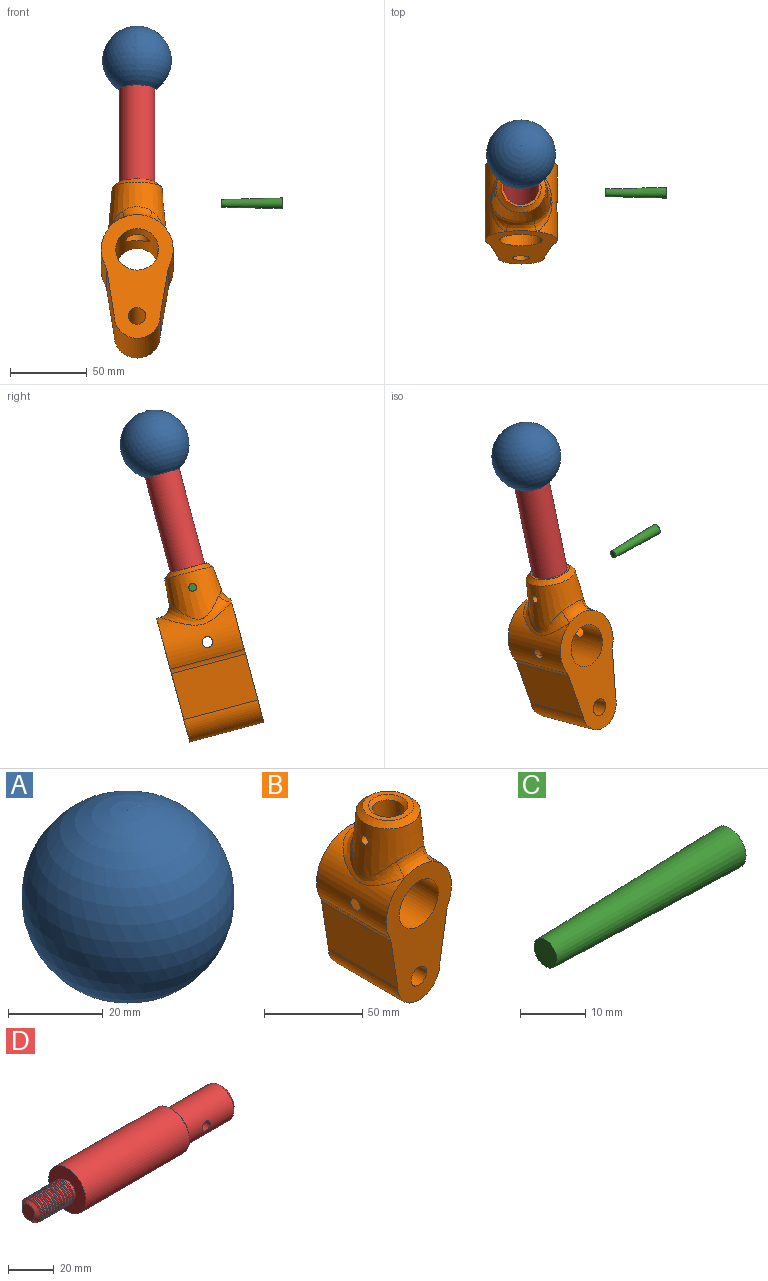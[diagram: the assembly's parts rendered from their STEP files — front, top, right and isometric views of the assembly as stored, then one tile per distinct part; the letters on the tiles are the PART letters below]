
ASSEMBLY  parts=4 mates=3
PART A: 8 faces, bbox 45.4x45.4x43.2 mm
  f0: sphere r=22.5mm, area 5937.6mm2, adj f1
  f1: plane 22.87x22.87mm, normal (0,0,-1), area 304.4mm2, adj f0,f3,f5,f6
  f2: cone r=0mm half-angle=59deg, axis (0,0,-1), area 97.2mm2, adj f3,f4
  f3: cylinder r=5.15mm len=34mm, axis (0,0,-1), area 433.4mm2, adj f1,f2,f5,f6,f7
  f4: cylinder r=5.15mm len=4.09mm, axis (0,0,1), area 0.6mm2, adj f2,f5,f7
  f5: bspline ~35.2x13.86mm, area 672mm2, adj f1,f3,f4,f6,f7
  f6: bspline ~34.62x13.86mm, area 657.8mm2, adj f1,f3,f5,f7
  f7: plane 0.98x0.68mm, normal (0.79,-0.61,0), area 0.4mm2, adj f3,f4,f5,f6
PART B: 21 faces, bbox 47x50x110 mm
  f0: cone r=16mm half-angle=5deg, axis (0,0,-1), area 2465.3mm2, adj f13,f14,f15,f19,f20
  f1: cylinder r=8mm len=36.51mm, axis (0,0,1), area 1715mm2, adj f2,f16,f19,f20
  f2: cylinder r=14mm len=50mm, axis (0,-1,0), area 4080.2mm2, adj f1,f8,f9,f17,f18
  f3: cylinder r=23.5mm len=50mm, axis (0,-1,0), area 2892.7mm2, adj f8,f9,f10,f11,f13,f17,f18
  f4: plane 50x31.11mm, normal (-0.99,0,-0.15), area 1574.5mm2, adj f5,f8,f9,f10
  f5: cylinder r=15mm len=50mm, axis (0,-1,0), area 2356.2mm2, adj f4,f6,f8,f9
  f6: plane 50x32.09mm, normal (0.99,0,-0.16), area 1626.1mm2, adj f5,f8,f9,f11
  f7: cylinder r=5.6mm len=50mm, axis (0,-1,0), area 1759.3mm2, adj f8,f9
  f8: plane 83.5x47mm, normal (0,1,0), area 2210.5mm2, adj f2,f3,f4,f5,f6,f7,f10,f11
  f9: plane 83.5x47mm, normal (0,-1,0), area 2210.5mm2, adj f2,f3,f4,f5,f6,f7,f10,f11
  f10: cylinder r=10mm len=50mm, axis (0,-1,0), area 161.9mm2, adj f3,f4,f8,f9
  f11: cylinder r=10mm len=50mm, axis (0,-1,0), area 142.6mm2, adj f3,f6,f8,f9
  f12: plane 26x26mm, normal (0,0,1), area 216.8mm2, adj f15,f16
  f13: bspline ~47.61x40.25mm, area 845.2mm2, adj f0,f3,f14
  f14: bspline ~21.62x9.1mm, area 169.5mm2, adj f0,f9,f13
  f15: cone r=13mm half-angle=47.5deg, axis (0,0,-1), area 406.7mm2, adj f0,f12
  f16: cone r=8mm half-angle=45deg, axis (0,0,1), area 159.9mm2, adj f1,f12
  f17: cone r=3.5mm half-angle=1.5deg, axis (1,0,0), area 276.2mm2, adj f2,f3
  f18: cone r=3.5mm half-angle=1.5deg, axis (1,0,0), area 219.3mm2, adj f2,f3
  f19: cone r=2.5mm half-angle=1.5deg, axis (1,0,0), area 190.1mm2, adj f0,f1
  f20: cone r=2.5mm half-angle=1.5deg, axis (1,0,0), area 153.5mm2, adj f0,f1
PART C: 3 faces, bbox 40x7x7 mm
  f0: plane 7.03x7.03mm, normal (1,0,0), area 38.9mm2, adj f1
  f1: cone r=2.5mm half-angle=1.5deg, axis (1,0,0), area 756.4mm2, adj f0,f2
  f2: plane 5x5mm, normal (-1,0,0), area 19.6mm2, adj f1
PART D: 17 faces, bbox 120x23x23 mm
  f0: cylinder r=11.5mm len=64mm, axis (-1,0,0), area 4624.4mm2, adj f1,f8
  f1: plane 23x23mm, normal (1,0,0), area 261.5mm2, adj f0,f2
  f2: cylinder r=7mm len=14mm, axis (-1,0,0), area 88mm2, adj f1,f3
  f3: plane 18x18mm, normal (-1,0,0), area 100.5mm2, adj f2,f5
  f4: plane 14x14mm, normal (1,0,0), area 153.9mm2, adj f6
  f5: cylinder r=9mm len=28mm, axis (1,0,0), area 1543.7mm2, adj f3,f6,f7
  f6: cone r=7mm half-angle=45deg, axis (-1,0,0), area 142.2mm2, adj f4,f5
  f7: cylinder r=2.5mm len=17.29mm, axis (0,-1,0), area 271.6mm2, adj f5
  f8: plane 23x23mm, normal (-1,0,0), area 336.9mm2, adj f0,f9
  f9: cylinder r=5mm len=10mm, axis (1,0,0), area 62.8mm2, adj f8,f10
  f10: plane 12x12mm, normal (1,0,0), area 34.6mm2, adj f9,f12
  f11: plane 8x8mm, normal (-1,0,0), area 50.3mm2, adj f16
  f12: cylinder r=6mm len=20mm, axis (-1,0,0), area 348.3mm2, adj f10,f13,f14,f15,f16
  f13: bspline ~21.2x13.86mm, area 396.6mm2, adj f12,f14,f15,f16
  f14: bspline ~21.2x13.86mm, area 385.9mm2, adj f12,f13,f15,f16
  f15: plane 0.98x0.77mm, normal (0,-0.43,0.9), area 0.4mm2, adj f12,f13,f14
  f16: cone r=4mm half-angle=45deg, axis (1,0,0), area 76.7mm2, adj f11,f12,f13,f14
PLACE A rot(axis=(-0.13,-0.13,-0.98),91deg) t=(31.6,80.83,163.69)mm
PLACE B rot(axis=(-1,0,0),15deg) t=(31.69,25.09,40.42)mm
PLACE C rot(axis=(-1,0,0),15deg) t=(104.98,55.92,70.46)mm
PLACE D rot(axis=(0.52,0.52,-0.68),111.8deg) t=(31.69,66.53,110.07)mm
MATE fastened D.f0 <-> A.f1  axis (0,0.26,0.97) through (31.69,75.85,144.84)mm
MATE cylindrical D.f0 <-> B.f0  axis (0,-0.26,-0.97) through (31.69,58.77,81.09)mm
MATE slider C.f1 <-> B.f19  axis (1,0,0) through (106.76,55.92,70.46)mm
